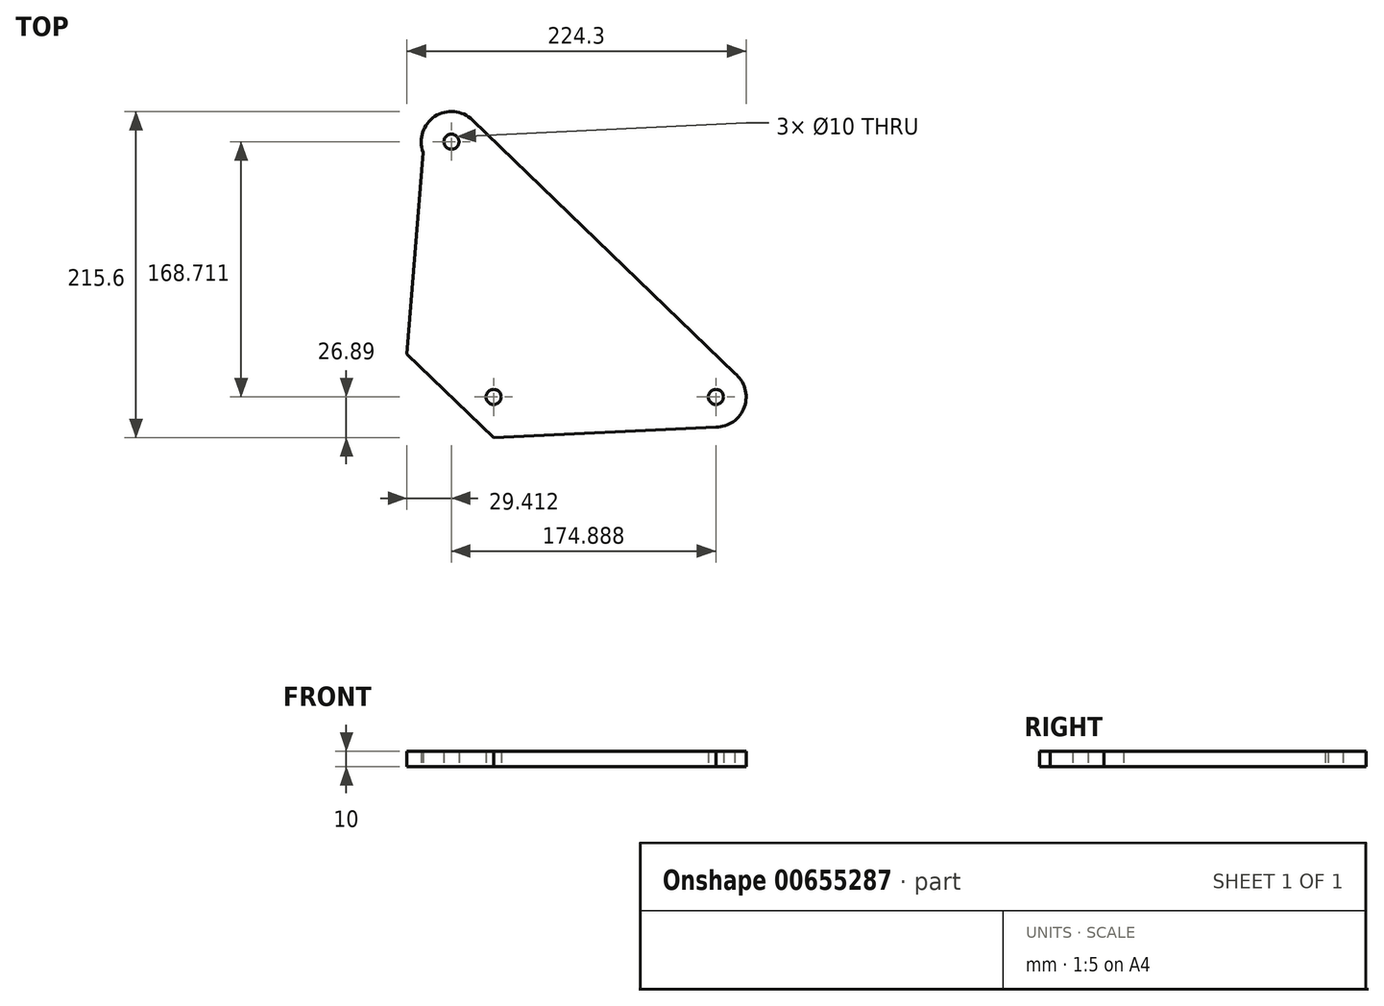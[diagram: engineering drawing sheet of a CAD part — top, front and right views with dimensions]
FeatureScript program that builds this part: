
annotation { "Feature Type Name" : "Feature", "Feature Type Description" : "" }
export const myFeature = defineFeature(function(context is Context, id is Id, definition is map)
    precondition{}
    {
        {
            var Q0;
            Q0=qCreatedBy(makeId("Top.planeOp"),FACE);
            var sketch = newSketch(context, id + "F0", { "sketchPlane" : qUnion([Q0])});
            skCircle(sketch, "E0", {"center": v(0, 0) * mm, "radius": 5 * mm});
            skCircle(sketch, "E1", {"center": v(-27.89, 168.71) * mm, "radius": 5 * mm});
            skCircle(sketch, "E2", {"center": v(147, 0) * mm, "radius": 5 * mm});
            skArc(sketch, "E3", {"start": v(-14, 183.1) * mm, "mid": v(-38.83, 185.45) * mm, "end": v(-46.64, 161.76) * mm});
            skArc(sketch, "E4", {"start": v(147, -20) * mm, "mid": v(165.89, -6.58) * mm, "end": v(159.43, 15.67) * mm});
            skLineSegment(sketch, "E5", {"start": v(159.43, 15.67) * mm, "end": v(-14, 183.1) * mm});
            skLineSegment(sketch, "E6", {"start": v(0, -26.89) * mm, "end": v(-57.3, 28.43) * mm});
            skLineSegment(sketch, "E7", {"start": v(-57.3, 28.43) * mm, "end": v(-46.64, 161.76) * mm});
            skLineSegment(sketch, "E8", {"start": v(0, -26.89) * mm, "end": v(147, -20) * mm});
            skSolve(sketch);
        }
        {
            var Q0;
            Q0=makeQuery(id+"F0.imprint","IMPRINT",FACE,{"disambiguationData":[TD([[makeQuery(id+"F0.imprint","IMPRINT",EDGE,{"derivedFrom":sQuery(id+"F0.wireOp",EDGE,"E0")}),-1.0]])]});
            extrude(context, id + "F1", {"entities" : qUnion([Q0]), "depth" : 10 * mm, "offsetDistance" : 25 * mm});
        }
    });
